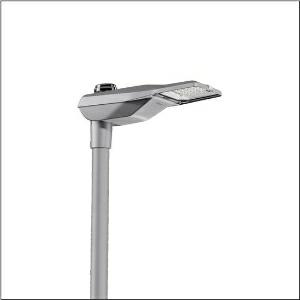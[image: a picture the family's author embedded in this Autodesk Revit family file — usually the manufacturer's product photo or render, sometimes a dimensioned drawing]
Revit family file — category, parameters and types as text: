
# Revit family: streetlight_sl_21_micro___st1_0a_5xe5d27n08db_a8cd
name_source: partatom
category: Lighting Fixtures
units: mm (PartAtom-declared; Revit-internal decimal feet)

## family parameters
Cut with Voids When Loaded = No
Host = Face
Light Source = No
Part Type = Normal
Room Calculation Point = No
Round Connector Dimension = Use Diameter
Shared = No

## types (1)
- --- (1 x LED, 4230 lm, 39.1 W, 2200K)
    Apparent Load = 39 VA
    CIE Flux Codes = 37 72 97 100 100
    Color Rendering = 70
    Color Temperature = 2200K
    Default Elevation = 1800 mm
    Description = Streetlight SL 21 micro, mast luminaire, primary light control with lens, of PMMA, primary optical cover: cover, of toughened safety glass, transparent, light distribution: ST1.0a, light emission: direct distribution, primary light characteristic: asymmetric, installation type: post-top, LED, 3G 1.5mm², High Power LED, rated luminous flux: 4.230lm, luminous efficacy: 108lm/W, light colour: 722, colour temperature: 2200K, control gear: NEMA (7pin), control: overheat protection, pre-setting: linear dimming characteristic, constant luminous flux control, time-dependent luminous flux control, flexible luminous flux parameterisation, mains connection: 230..240V, AC, 50/60Hz, connection cable pre-assembled, cable length: 6,5m, wiring characteristics: H07RN-F, start of lifetime: 39W, end of service life: 41W, reduction: 18W, luminaire housing, of diecast aluminium (EN AC-44300), powder-coated, Siteco® metallic grey (DB 702S), corrosivity category C5 mid according to DIN EN ISO 12944, multi-level sealing system, sealing non-destructively replaceable, inclination adjustable: 0°, 5°, 10°, 15°, length: 528mm, width: 235mm, height: 110mm, spigot size: 76/60mm (post-top), mounting height: 4..8m, protection rating (complete): IP66, insulation class (complete): insulation class I (protective earthing), certification: CE, ENEC, ENEC+, VDE, impact resistance: IK10, permissible operating ambient temperature for outdoor applications: -40..+50°C, standard-compliant lighting for roads and squares, packaging unit: 1 piece

Light Distribution: ST1.0a
    Height = 110 mm
    Lamp = 1 x LED
    Lamp Light Flux = 4230 lm
    Lamp Power = 39.1 W
    Lamp count = 1
    Length = 528 mm
    Luminous efficacy = 108 lm/W
    Manufacturer = Siteco
    ModVariant = No
    Model = 5XE5D27N08DB
    Number of Poles = 1
    OnlyDefault = Yes
    Power Factor = 1
    Product Name = Streetlight SL 21 micro | ST1.0a
    Product group = mast luminaire | pylon top
    ProductGroupID = 6100
    Protection Class = Protection class I
    Protection Degree = IP 66
    RLX_Detail_Level = 1
    RLX_Emergency_Light_Flux = 0 lm
    RLX_Emergency_Type = 0
    RLX_Emergency_Type_DB = No
    RlxData = <blob elided: 98493 chars, md5=14d1b149>
    Socket = socket
    Standby Power = 0 W
    System Light Flux = 4230 lm
    System Power = 39 W
    Type Comments = factory setting: luminous flux: 100 % | dim-lin: 254 | 765 mA
    Type Image = l_1294375.jpg
    URL = http://relux.com
    VarID = @adj_136616
    Voltage = 0 V
    Weight = 0.00 kg
    Width = 235 mm

## geometry (parser evidence)
native form markers: Blend x4, Sweep x11
no freeform markers — native parametric forms only
